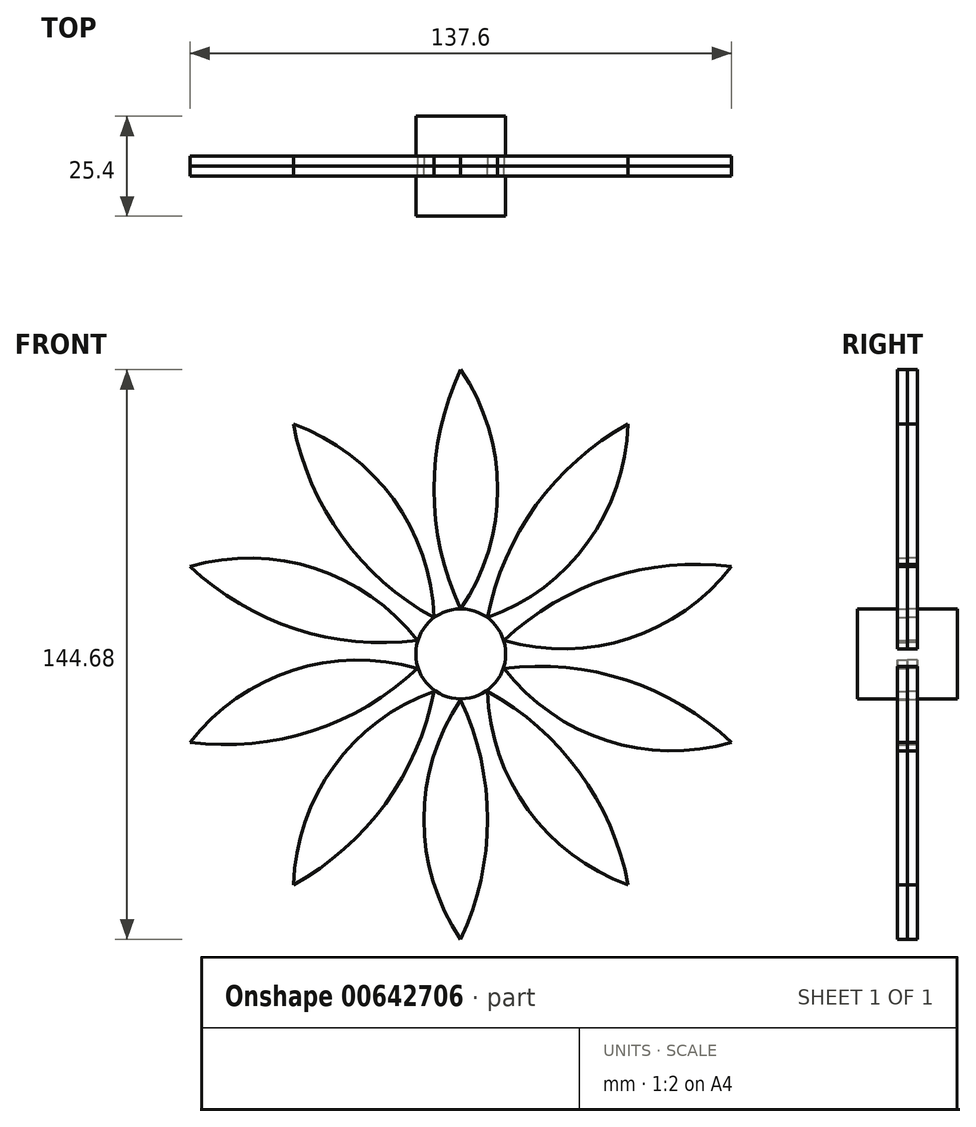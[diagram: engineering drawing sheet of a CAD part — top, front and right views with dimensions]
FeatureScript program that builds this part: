
annotation { "Feature Type Name" : "Feature", "Feature Type Description" : "" }
export const myFeature = defineFeature(function(context is Context, id is Id, definition is map)
    precondition{}
    {
        {
            var Q0;
            Q0=qCreatedBy(makeId("Front.planeOp"),FACE);
            var sketch = newSketch(context, id + "F0", { "sketchPlane" : qUnion([Q0])});
            skCircle(sketch, "E0", {"center": v(0, 0) * mm, "radius": 11.42 * mm});
            skArc(sketch, "E1", {"start": v(0, 72.2) * mm, "mid": v(-6.8, 41.8) * mm, "end": v(0, 11.42) * mm});
            skArc(sketch, "E2", {"start": v(0, 11.42) * mm, "mid": v(9.36, 41.8) * mm, "end": v(0, 72.2) * mm});
            skArc(sketch, "E3.1.0", {"start": v(-42.52, 58.38) * mm, "mid": v(-30.16, 29.8) * mm, "end": v(-6.8, 9.21) * mm});
            skArc(sketch, "E3.1.1", {"start": v(-6.8, 9.21) * mm, "mid": v(-17.08, 39.3) * mm, "end": v(-42.52, 58.38) * mm});
            skArc(sketch, "E3.2.0", {"start": v(-68.8, 22.2) * mm, "mid": v(-42, 6.35) * mm, "end": v(-11, 3.43) * mm});
            skArc(sketch, "E3.2.1", {"start": v(-11, 3.43) * mm, "mid": v(-37, 21.72) * mm, "end": v(-68.8, 22.2) * mm});
            skArc(sketch, "E3.3.0", {"start": v(-68.8, -22.5) * mm, "mid": v(-37.8, -19.58) * mm, "end": v(-11, -3.72) * mm});
            skArc(sketch, "E3.3.1", {"start": v(-11, -3.72) * mm, "mid": v(-42.8, -4.2) * mm, "end": v(-68.8, -22.5) * mm});
            skArc(sketch, "E3.4.0", {"start": v(-42.52, -58.67) * mm, "mid": v(-19.16, -38.08) * mm, "end": v(-6.8, -9.5) * mm});
            skArc(sketch, "E3.4.1", {"start": v(-6.8, -9.5) * mm, "mid": v(-32.23, -28.58) * mm, "end": v(-42.52, -58.67) * mm});
            skArc(sketch, "E3.5.0", {"start": v(0, -72.49) * mm, "mid": v(6.8, -42.1) * mm, "end": v(0, -11.71) * mm});
            skArc(sketch, "E3.5.1", {"start": v(0, -11.71) * mm, "mid": v(-9.36, -42.1) * mm, "end": v(0, -72.49) * mm});
            skArc(sketch, "E3.6.0", {"start": v(42.52, -58.67) * mm, "mid": v(30.16, -30.1) * mm, "end": v(6.8, -9.5) * mm});
            skArc(sketch, "E3.6.1", {"start": v(6.8, -9.5) * mm, "mid": v(17.08, -39.6) * mm, "end": v(42.52, -58.67) * mm});
            skArc(sketch, "E3.7.0", {"start": v(68.8, -22.5) * mm, "mid": v(42, -6.64) * mm, "end": v(11, -3.72) * mm});
            skArc(sketch, "E3.7.1", {"start": v(11, -3.72) * mm, "mid": v(37, -22.01) * mm, "end": v(68.8, -22.5) * mm});
            skArc(sketch, "E3.8.0", {"start": v(68.8, 22.2) * mm, "mid": v(37.8, 19.28) * mm, "end": v(11, 3.43) * mm});
            skArc(sketch, "E3.8.1", {"start": v(11, 3.43) * mm, "mid": v(42.8, 3.91) * mm, "end": v(68.8, 22.2) * mm});
            skArc(sketch, "E3.9.0", {"start": v(42.52, 58.38) * mm, "mid": v(19.16, 37.8) * mm, "end": v(6.8, 9.21) * mm});
            skArc(sketch, "E3.9.1", {"start": v(6.8, 9.21) * mm, "mid": v(32.23, 28.3) * mm, "end": v(42.52, 58.38) * mm});
            skPoint(sketch, "E3.center", {"position": v(0, -0.15) * mm});
            skSolve(sketch);
        }
        {
            var Q0;
            Q0=makeQuery(id+"F0.imprint","IMPRINT",FACE,{"disambiguationData":[TD([[makeQuery(id+"F0.imprint","IMPRINT",EDGE,{"derivedFrom":sQuery(id+"F0.wireOp",EDGE,"E0")}),1.0]])]});
            extrude(context, id + "F1", {"entities" : qUnion([Q0]), "depth" : 12.7 * mm, "offsetDistance" : 25.4 * mm});
        }
        {
            var Q0;
            Q0=makeQuery(id+"F1.opExtrude","SWEPT_BODY",BODY,{"disambiguationData":[OSD([sQuery(id+"F0.wireOp",EDGE,"E0")])]});
            var Q1;
            Q1=qCreatedBy(makeId("Front.planeOp"),FACE);
            mirror(context, id + "F2", {"operationType" : NewBodyOperationType.ADD, "entities" : qUnion([Q0]), "mirrorPlane" : qUnion([Q1])});
        }
        {
            var Q0;
            Q0 = qSketchRegion(id + "F0", true);
            extrude(context, id + "F3", {"entities" : qUnion([Q0]), "operationType" : NewBodyOperationType.ADD, "depth" : 2.54 * mm, "offsetDistance" : 25.4 * mm});
        }
        {
            var Q0;
            Q0=makeQuery(id+"F3.opExtrude","SWEPT_BODY",BODY,{"disambiguationData":[OSD([sQuery(id+"F0.wireOp",EDGE,"E3.8.0"),sQuery(id+"F0.wireOp",EDGE,"E3.8.1")])]});
            var Q1;
            Q1=makeQuery(id+"F3.opExtrude","SWEPT_BODY",BODY,{"disambiguationData":[OSD([sQuery(id+"F0.wireOp",EDGE,"E3.7.0"),sQuery(id+"F0.wireOp",EDGE,"E3.7.1")])]});
            var Q2;
            Q2=makeQuery(id+"F3.opExtrude","SWEPT_BODY",BODY,{"disambiguationData":[OSD([sQuery(id+"F0.wireOp",EDGE,"E3.6.0"),sQuery(id+"F0.wireOp",EDGE,"E3.6.1")])]});
            var Q3;
            Q3=makeQuery(id+"F3.opExtrude","SWEPT_BODY",BODY,{"disambiguationData":[OSD([sQuery(id+"F0.wireOp",EDGE,"E3.5.0"),sQuery(id+"F0.wireOp",EDGE,"E3.5.1")])]});
            var Q4;
            Q4=makeQuery(id+"F3.opExtrude","SWEPT_BODY",BODY,{"disambiguationData":[OSD([sQuery(id+"F0.wireOp",EDGE,"E3.4.0"),sQuery(id+"F0.wireOp",EDGE,"E3.4.1")])]});
            var Q5;
            Q5=makeQuery(id+"F3.opExtrude","SWEPT_BODY",BODY,{"disambiguationData":[OSD([sQuery(id+"F0.wireOp",EDGE,"E3.3.0"),sQuery(id+"F0.wireOp",EDGE,"E3.3.1")])]});
            var Q6;
            Q6=makeQuery(id+"F3.opExtrude","SWEPT_BODY",BODY,{"disambiguationData":[OSD([sQuery(id+"F0.wireOp",EDGE,"E3.2.0"),sQuery(id+"F0.wireOp",EDGE,"E3.2.1")])]});
            var Q7;
            Q7=makeQuery(id+"F3.opExtrude","SWEPT_BODY",BODY,{"disambiguationData":[OSD([sQuery(id+"F0.wireOp",EDGE,"E3.1.0"),sQuery(id+"F0.wireOp",EDGE,"E3.1.1")])]});
            var Q8;
            {var subQ0=sQuery(id+"F0.wireOp",EDGE,"E0");Q8=makeQuery(id+"F3.boolean.opBoolean","MERGE",BODY,{"derivedFrom":[makeQuery(id+"F1.opExtrude","SWEPT_BODY",BODY,{"disambiguationData":[OSD([subQ0])]}),makeQuery(id+"F3.opExtrude","SWEPT_BODY",BODY,{"disambiguationData":[OSD([subQ0])]}),makeQuery(id+"F3.opExtrude","SWEPT_BODY",BODY,{"disambiguationData":[OSD([sQuery(id+"F0.wireOp",EDGE,"E1"),sQuery(id+"F0.wireOp",EDGE,"E2")])]})]});}
            var Q9;
            Q9=makeQuery(id+"F3.opExtrude","SWEPT_BODY",BODY,{"disambiguationData":[OSD([sQuery(id+"F0.wireOp",EDGE,"E3.9.0"),sQuery(id+"F0.wireOp",EDGE,"E3.9.1")])]});
            var Q10;
            Q10=qCreatedBy(makeId("Front.planeOp"),FACE);
            mirror(context, id + "F4", {"entities" : qUnion([Q0, Q1, Q2, Q3, Q4, Q5, Q6, Q7, Q8, Q9]), "mirrorPlane" : qUnion([Q10])});
        }
    });
